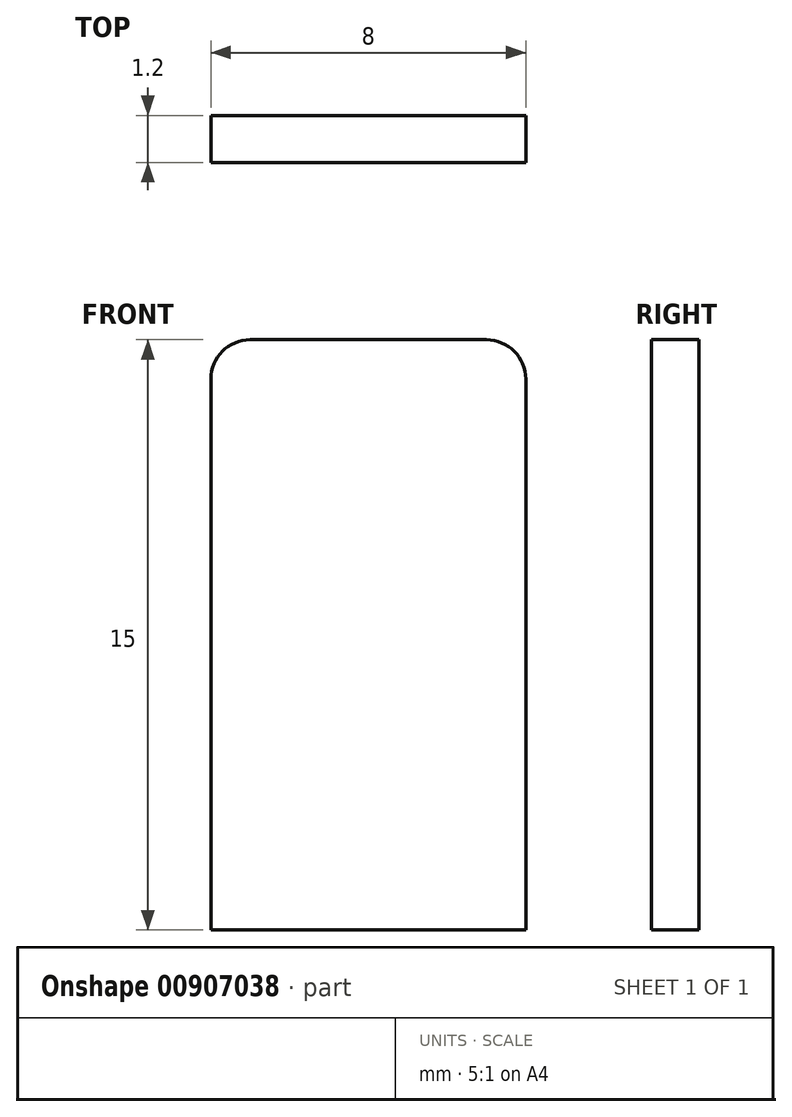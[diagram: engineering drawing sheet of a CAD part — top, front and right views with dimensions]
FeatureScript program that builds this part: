
annotation { "Feature Type Name" : "Feature", "Feature Type Description" : "" }
export const myFeature = defineFeature(function(context is Context, id is Id, definition is map)
    precondition{}
    {
        {
            var Q0;
            Q0=qCreatedBy(makeId("Front.planeOp"),FACE);
            var sketch = newSketch(context, id + "F0", { "sketchPlane" : qUnion([Q0])});
            skLineSegment(sketch, "E0.bottom", {"start": v(0, 0) * mm, "end": v(8, 0) * mm});
            skLineSegment(sketch, "E0.top", {"start": v(0, 15) * mm, "end": v(8, 15) * mm});
            skLineSegment(sketch, "E0.left", {"start": v(0, 0) * mm, "end": v(0, 15) * mm});
            skLineSegment(sketch, "E0.right", {"start": v(8, 0) * mm, "end": v(8, 15) * mm});
            skSolve(sketch);
        }
        {
            var Q0;
            Q0=makeQuery(id+"F0.imprint","IMPRINT",FACE,{"disambiguationData":[TD([[makeQuery(id+"F0.imprint","IMPRINT",EDGE,{"derivedFrom":sQuery(id+"F0.wireOp",EDGE,"E0.bottom")}),1.0]])]});
            extrude(context, id + "F1", {"entities" : qUnion([Q0]), "depth" : 1.2 * mm, "offsetDistance" : 25 * mm});
        }
        {
            var Q0;
            Q0=makeQuery(id+"F1.opExtrude","SWEPT_EDGE",EDGE,{"disambiguationData":[OSD([sQuery(id+"F0.wireOp",EDGE,"E0.top"),sQuery(id+"F0.wireOp",EDGE,"E0.left")])]});
            var Q1;
            Q1=makeQuery(id+"F1.opExtrude","SWEPT_EDGE",EDGE,{"disambiguationData":[OSD([sQuery(id+"F0.wireOp",EDGE,"E0.top"),sQuery(id+"F0.wireOp",EDGE,"E0.right")])]});
            fillet(context, id + "F2", {"entities" : qUnion([Q0, Q1]), "radius" : 1 * mm, "tangentPropagation" : true, "allowEdgeOverflow" : false});
        }
    });
